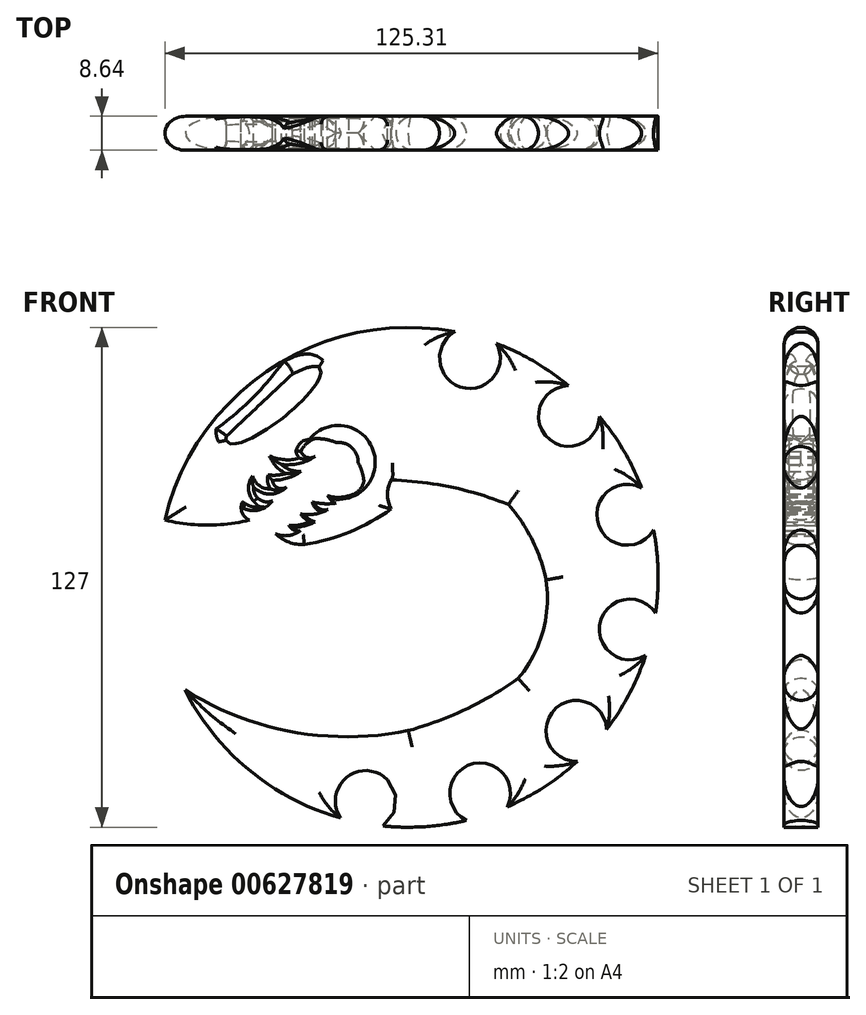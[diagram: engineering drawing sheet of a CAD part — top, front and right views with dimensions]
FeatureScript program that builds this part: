
annotation { "Feature Type Name" : "Feature", "Feature Type Description" : "" }
export const myFeature = defineFeature(function(context is Context, id is Id, definition is map)
    precondition{}
    {
        {
            var Q0;
            Q0=qCreatedBy(makeId("Front.planeOp"),FACE);
            var sketch = newSketch(context, id + "F0", { "sketchPlane" : qUnion([Q0])});
            skArc(sketch, "E0", {"start": v(11.85, 62.39) * mm, "mid": v(-34.6, 53.25) * mm, "end": v(-61.81, 14.54) * mm});
            skArc(sketch, "E1", {"start": v(11.85, 62.39) * mm, "mid": v(13.6, 48.25) * mm, "end": v(22.46, 59.4) * mm});
            skArc(sketch, "E2.1.0", {"start": v(40.75, 48.7) * mm, "mid": v(35.38, 35.5) * mm, "end": v(48.56, 40.92) * mm});
            skArc(sketch, "E2.2.0", {"start": v(59.32, 22.67) * mm, "mid": v(48.2, 13.76) * mm, "end": v(62.34, 12.07) * mm});
            skArc(sketch, "E2.3.0", {"start": v(62.84, -9.11) * mm, "mid": v(48.8, -11.47) * mm, "end": v(60.32, -19.85) * mm});
            skArc(sketch, "E2.4.0", {"start": v(50.43, -38.59) * mm, "mid": v(37.02, -33.8) * mm, "end": v(43, -46.73) * mm});
            skArc(sketch, "E2.5.0", {"start": v(25.23, -58.27) * mm, "mid": v(15.85, -47.55) * mm, "end": v(14.77, -61.76) * mm});
            skArc(sketch, "E2.6.0", {"start": v(-6.36, -63.18) * mm, "mid": v(-9.33, -49.25) * mm, "end": v(-17.2, -61.13) * mm});
            skLineSegment(sketch, "E2.anchor1", {"start": v(0, 0) * mm, "end": v(15.69, 55.68) * mm, "construction": true});
            skLineSegment(sketch, "E2.anchor2", {"start": v(0, 0) * mm, "end": v(-10.77, -56.84) * mm, "construction": true});
            skArc(sketch, "E3.trimOffspring", {"start": v(40.75, 48.7) * mm, "mid": v(32.05, 54.82) * mm, "end": v(22.46, 59.4) * mm});
            skArc(sketch, "E4.trimOffspring", {"start": v(59.32, 22.67) * mm, "mid": v(54.7, 32.25) * mm, "end": v(48.56, 40.92) * mm});
            skArc(sketch, "E5.trimOffspring", {"start": v(62.84, -9.11) * mm, "mid": v(63.48, 1.5) * mm, "end": v(62.34, 12.07) * mm});
            skArc(sketch, "E6.trimOffspring", {"start": v(50.43, -38.59) * mm, "mid": v(56.16, -29.63) * mm, "end": v(60.32, -19.85) * mm});
            skArc(sketch, "E7.trimOffspring", {"start": v(25.23, -58.27) * mm, "mid": v(34.6, -53.25) * mm, "end": v(43, -46.73) * mm});
            skArc(sketch, "E8.trimOffspring", {"start": v(-6.36, -63.18) * mm, "mid": v(4.26, -63.36) * mm, "end": v(14.77, -61.76) * mm});
            skPoint(sketch, "E9.endSnap0", {"position": v(-61.81, 14.54) * mm});
            skArc(sketch, "E10", {"start": v(-33.7, 11.06) * mm, "mid": v(-30.33, 8.93) * mm, "end": v(-26.4, 8.38) * mm});
            skArc(sketch, "E11", {"start": v(-11.26, 24.4) * mm, "mid": v(-15.29, 32.32) * mm, "end": v(-23.7, 35.21) * mm});
            skArc(sketch, "E12", {"start": v(-61.81, 14.54) * mm, "mid": v(-51.03, 13.27) * mm, "end": v(-40.25, 14.54) * mm});
            skPoint(sketch, "E12.endSnap0", {"position": v(-52.38, 14.54) * mm});
            skArc(sketch, "E13", {"start": v(-42.42, 17.84) * mm, "mid": v(-41.86, 15.84) * mm, "end": v(-40.25, 14.54) * mm});
            skArc(sketch, "E14", {"start": v(-42.42, 17.84) * mm, "mid": v(-38.16, 17.08) * mm, "end": v(-34.5, 19.4) * mm});
            skArc(sketch, "E15", {"start": v(-39.31, 22.94) * mm, "mid": v(-37.88, 19.85) * mm, "end": v(-34.5, 19.4) * mm});
            skArc(sketch, "E16", {"start": v(-39.31, 22.94) * mm, "mid": v(-35.13, 21.15) * mm, "end": v(-30.94, 22.94) * mm});
            skArc(sketch, "E17", {"start": v(-34.5, 24.67) * mm, "mid": v(-33.23, 22.76) * mm, "end": v(-30.94, 22.94) * mm});
            skArc(sketch, "E18", {"start": v(-34.5, 24.67) * mm, "mid": v(-30.67, 25.18) * mm, "end": v(-27.22, 26.94) * mm});
            skArc(sketch, "E19", {"start": v(-32.24, 28.7) * mm, "mid": v(-29.91, 27.3) * mm, "end": v(-27.22, 26.94) * mm});
            skArc(sketch, "E20", {"start": v(-32.24, 28.7) * mm, "mid": v(-27.78, 28.9) * mm, "end": v(-23.7, 30.7) * mm});
            skArc(sketch, "E21", {"start": v(-27.22, 32) * mm, "mid": v(-25.78, 30.5) * mm, "end": v(-23.7, 30.7) * mm});
            skPoint(sketch, "E9.end.orphan", {"position": v(-42.95, 14.54) * mm});
            skArc(sketch, "E22", {"start": v(-23.7, 35.21) * mm, "mid": v(-25.8, 33.98) * mm, "end": v(-27.22, 32) * mm});
            skEllipticalArc(sketch, "E23", {});
            skLineSegment(sketch, "E24", {"start": v(-46.15, 35.91) * mm, "end": v(-29.44, 51.63) * mm});
            skArc(sketch, "E25", {"start": v(-33.7, 11.06) * mm, "mid": v(-30.4, 10.62) * mm, "end": v(-27.33, 11.89) * mm});
            skArc(sketch, "E26", {"start": v(-30.22, 13.12) * mm, "mid": v(-29.01, 11.95) * mm, "end": v(-27.33, 11.89) * mm});
            skArc(sketch, "E27", {"start": v(-30.22, 13.12) * mm, "mid": v(-27.54, 13.33) * mm, "end": v(-24.95, 14.07) * mm});
            skArc(sketch, "E28", {"start": v(-27.33, 16.1) * mm, "mid": v(-26.24, 14.96) * mm, "end": v(-24.95, 14.07) * mm});
            skArc(sketch, "E29", {"start": v(-27.33, 16.1) * mm, "mid": v(-24.47, 15.96) * mm, "end": v(-21.68, 16.63) * mm});
            skArc(sketch, "E30", {"start": v(-24.36, 19.13) * mm, "mid": v(-23.42, 17.45) * mm, "end": v(-21.68, 16.63) * mm});
            skArc(sketch, "E31", {"start": v(-24.36, 19.13) * mm, "mid": v(-21.37, 18.7) * mm, "end": v(-18.35, 18.83) * mm});
            skPoint(sketch, "E32", {"position": v(-56.68, -28.62) * mm});
            skArc(sketch, "E33", {"start": v(-20.45, 20.72) * mm, "mid": v(-19.57, 19.59) * mm, "end": v(-18.35, 18.83) * mm});
            skArc(sketch, "E34", {"start": v(-20.45, 20.72) * mm, "mid": v(-17.77, 20.3) * mm, "end": v(-15.1, 20.72) * mm});
            skArc(sketch, "E35", {"start": v(-15.1, 20.72) * mm, "mid": v(-12.6, 21.96) * mm, "end": v(-11.26, 24.4) * mm});
            skArc(sketch, "E36", {"start": v(-56.68, -28.62) * mm, "mid": v(-29.34, -39.26) * mm, "end": v(0, -38.95) * mm});
            skArc(sketch, "E37", {"start": v(35.04, -0.67) * mm, "mid": v(31.48, 9.53) * mm, "end": v(25.45, 18.5) * mm});
            skArc(sketch, "E38", {"start": v(25.45, 18.5) * mm, "mid": v(10.84, 22.95) * mm, "end": v(-4.33, 24.71) * mm});
            skArc(sketch, "E39.trimOffspring", {"start": v(-56.68, -28.62) * mm, "mid": v(-40.36, -49.03) * mm, "end": v(-17.2, -61.13) * mm});
            skPoint(sketch, "E40.visualSharp", {"position": v(25.45, 18.5) * mm});
            skPoint(sketch, "E41.visualSharp", {"position": v(34.66, -19.7) * mm});
            skArc(sketch, "E42", {"start": v(27.93, -25.71) * mm, "mid": v(34.17, -13.96) * mm, "end": v(35.04, -0.67) * mm});
            skArc(sketch, "E43", {"start": v(0, -38.95) * mm, "mid": v(14.55, -33.56) * mm, "end": v(27.93, -25.71) * mm});
            skArc(sketch, "E44", {"start": v(-4.33, 24.71) * mm, "mid": v(-5.26, 21.05) * mm, "end": v(-4.33, 17.38) * mm});
            skArc(sketch, "E45", {"start": v(-26.4, 8.38) * mm, "mid": v(-14.81, 11.53) * mm, "end": v(-4.33, 17.38) * mm});
            const initialGuessF0  = {"E23": [-0.034181974582248115, 0.0437263421637328, -0.7832888515343989, -0.6216579244744834, 0.015090807915705154, 0.003951191540584326, 5.94360859800535, 4.104168110363256]};
            skSetInitialGuess(sketch, initialGuessF0);
            skSolve(sketch);
        }
        {
            var Q0;
            Q0 = qSketchRegion(id + "F0", true);
            extrude(context, id + "F1", {"entities" : qUnion([Q0]), "depth" : 25.4 * mm, "offsetDistance" : 25.4 * mm});
        }
        {
            var Q0;
            Q0=makeQuery(id+"F1.opExtrude","CAP_EDGE",EDGE,{"disambiguationData":[OSD([sQuery(id+"F0.wireOp",EDGE,"E0")])],"isStart":false});
            var Q1;
            Q1=makeQuery(id+"F1.opExtrude","CAP_EDGE",EDGE,{"disambiguationData":[OSD([sQuery(id+"F0.wireOp",EDGE,"E36")])],"isStart":false});
            var Q2;
            Q2=makeQuery(id+"F1.opExtrude","CAP_EDGE",EDGE,{"disambiguationData":[OSD([sQuery(id+"F0.wireOp",EDGE,"E37")])],"isStart":false});
            var Q3;
            Q3=makeQuery(id+"F1.opExtrude","CAP_EDGE",EDGE,{"disambiguationData":[OSD([sQuery(id+"F0.wireOp",EDGE,"E42")])],"isStart":false});
            var Q4;
            Q4=makeQuery(id+"F1.opExtrude","CAP_EDGE",EDGE,{"disambiguationData":[OSD([sQuery(id+"F0.wireOp",EDGE,"E43")])],"isStart":false});
            var Q5;
            Q5=makeQuery(id+"F1.opExtrude","CAP_EDGE",EDGE,{"disambiguationData":[OSD([sQuery(id+"F0.wireOp",EDGE,"E1")])],"isStart":false});
            var Q6;
            Q6=makeQuery(id+"F1.opExtrude","CAP_EDGE",EDGE,{"disambiguationData":[OSD([sQuery(id+"F0.wireOp",EDGE,"E3.trimOffspring")])],"isStart":false});
            var Q7;
            Q7=makeQuery(id+"F1.opExtrude","CAP_EDGE",EDGE,{"disambiguationData":[OSD([sQuery(id+"F0.wireOp",EDGE,"E2.1.0")])],"isStart":false});
            var Q8;
            Q8=makeQuery(id+"F1.opExtrude","CAP_EDGE",EDGE,{"disambiguationData":[OSD([sQuery(id+"F0.wireOp",EDGE,"E4.trimOffspring")])],"isStart":false});
            var Q9;
            Q9=makeQuery(id+"F1.opExtrude","CAP_EDGE",EDGE,{"disambiguationData":[OSD([sQuery(id+"F0.wireOp",EDGE,"E2.2.0")])],"isStart":false});
            var Q10;
            Q10=makeQuery(id+"F1.opExtrude","CAP_EDGE",EDGE,{"disambiguationData":[OSD([sQuery(id+"F0.wireOp",EDGE,"E2.3.0")])],"isStart":false});
            var Q11;
            Q11=makeQuery(id+"F1.opExtrude","CAP_EDGE",EDGE,{"disambiguationData":[OSD([sQuery(id+"F0.wireOp",EDGE,"E2.4.0")])],"isStart":false});
            var Q12;
            Q12=makeQuery(id+"F1.opExtrude","CAP_EDGE",EDGE,{"disambiguationData":[OSD([sQuery(id+"F0.wireOp",EDGE,"E6.trimOffspring")])],"isStart":false});
            var Q13;
            Q13=makeQuery(id+"F1.opExtrude","CAP_EDGE",EDGE,{"disambiguationData":[OSD([sQuery(id+"F0.wireOp",EDGE,"E7.trimOffspring")])],"isStart":false});
            var Q14;
            Q14=makeQuery(id+"F1.opExtrude","CAP_EDGE",EDGE,{"disambiguationData":[OSD([sQuery(id+"F0.wireOp",EDGE,"E2.6.0")])],"isStart":false});
            var Q15;
            Q15=makeQuery(id+"F1.opExtrude","CAP_EDGE",EDGE,{"disambiguationData":[OSD([sQuery(id+"F0.wireOp",EDGE,"E2.5.0")])],"isStart":false});
            var Q16;
            Q16=makeQuery(id+"F1.opExtrude","CAP_EDGE",EDGE,{"disambiguationData":[OSD([sQuery(id+"F0.wireOp",EDGE,"E12")])],"isStart":false});
            var Q17;
            Q17=makeQuery(id+"F1.opExtrude","CAP_EDGE",EDGE,{"disambiguationData":[OSD([sQuery(id+"F0.wireOp",EDGE,"E39.trimOffspring")])],"isStart":false});
            var Q18;
            Q18=makeQuery(id+"F1.opExtrude","CAP_EDGE",EDGE,{"disambiguationData":[OSD([sQuery(id+"F0.wireOp",EDGE,"E38")])],"isStart":false});
            fillet(context, id + "F2", {"entities" : qUnion([Q0, Q1, Q2, Q3, Q4, Q5, Q6, Q7, Q8, Q9, Q10, Q11, Q12, Q13, Q14, Q15, Q16, Q17, Q18]), "radius" : 4.32 * mm, "tangentPropagation" : true, "allowEdgeOverflow" : false});
        }
        {
            var Q0;
            Q0=makeQuery(id+"F1.opExtrude","CAP_EDGE",EDGE,{"disambiguationData":[OSD([sQuery(id+"F0.wireOp",EDGE,"E24")])],"isStart":false});
            var Q1;
            Q1=makeQuery(id+"F2.opFillet","BLEND_EDGE",EDGE,{"blendedFrom":[makeQuery(id+"F1.opExtrude","CAP_EDGE",EDGE,{"disambiguationData":[OSD([sQuery(id+"F0.wireOp",EDGE,"E0")])],"isStart":false}),makeQuery(id+"F1.opExtrude","SWEPT_FACE",FACE,{"disambiguationData":[OSD([sQuery(id+"F0.wireOp",EDGE,"E23")])]})],"blendedInto":[makeQuery(id+"F1.opExtrude","SWEPT_FACE",FACE,{"disambiguationData":[OSD([sQuery(id+"F0.wireOp",EDGE,"E23")])]})]});
            var Q2;
            Q2=makeQuery(id+"F1.opExtrude","CAP_EDGE",EDGE,{"disambiguationData":[OSD([sQuery(id+"F0.wireOp",EDGE,"E23")])],"isStart":false});
            var Q3;
            Q3=makeQuery(id+"F2.opFillet","BLEND_EDGE",EDGE,{"blendedFrom":[makeQuery(id+"F1.opExtrude","CAP_EDGE",EDGE,{"disambiguationData":[OSD([sQuery(id+"F0.wireOp",EDGE,"E0")])],"isStart":false}),makeQuery(id+"F1.opExtrude","SWEPT_FACE",FACE,{"disambiguationData":[OSD([sQuery(id+"F0.wireOp",EDGE,"E24")])]})],"blendedInto":[makeQuery(id+"F1.opExtrude","SWEPT_FACE",FACE,{"disambiguationData":[OSD([sQuery(id+"F0.wireOp",EDGE,"E24")])]})]});
            fillet(context, id + "F3", {"entities" : qUnion([Q0, Q1, Q2, Q3]), "radius" : 1.98 * mm, "tangentPropagation" : true, "allowEdgeOverflow" : false});
        }
        {
            var Q0;
            Q0=makeQuery(id+"F1.opExtrude","CAP_EDGE",EDGE,{"disambiguationData":[OSD([sQuery(id+"F0.wireOp",EDGE,"E16")])],"isStart":false});
            var Q1;
            Q1=makeQuery(id+"F1.opExtrude","CAP_EDGE",EDGE,{"disambiguationData":[OSD([sQuery(id+"F0.wireOp",EDGE,"E17")])],"isStart":false});
            var Q2;
            Q2=makeQuery(id+"F1.opExtrude","CAP_EDGE",EDGE,{"disambiguationData":[OSD([sQuery(id+"F0.wireOp",EDGE,"E18")])],"isStart":false});
            var Q3;
            Q3=makeQuery(id+"F1.opExtrude","CAP_EDGE",EDGE,{"disambiguationData":[OSD([sQuery(id+"F0.wireOp",EDGE,"E19")])],"isStart":false});
            var Q4;
            Q4=makeQuery(id+"F1.opExtrude","CAP_EDGE",EDGE,{"disambiguationData":[OSD([sQuery(id+"F0.wireOp",EDGE,"E20")])],"isStart":false});
            var Q5;
            Q5=makeQuery(id+"F1.opExtrude","CAP_EDGE",EDGE,{"disambiguationData":[OSD([sQuery(id+"F0.wireOp",EDGE,"E21")])],"isStart":false});
            var Q6;
            Q6=makeQuery(id+"F1.opExtrude","CAP_EDGE",EDGE,{"disambiguationData":[OSD([sQuery(id+"F0.wireOp",EDGE,"E15")])],"isStart":false});
            var Q7;
            Q7=makeQuery(id+"F2.opFillet","BLEND_EDGE",EDGE,{"blendedFrom":[makeQuery(id+"F1.opExtrude","CAP_EDGE",EDGE,{"disambiguationData":[OSD([sQuery(id+"F0.wireOp",EDGE,"E12")])],"isStart":false}),makeQuery(id+"F1.opExtrude","SWEPT_FACE",FACE,{"disambiguationData":[OSD([sQuery(id+"F0.wireOp",EDGE,"E14")])]})],"blendedInto":[makeQuery(id+"F1.opExtrude","SWEPT_FACE",FACE,{"disambiguationData":[OSD([sQuery(id+"F0.wireOp",EDGE,"E14")])]})]});
            var Q8;
            Q8=makeQuery(id+"F1.opExtrude","CAP_EDGE",EDGE,{"disambiguationData":[OSD([sQuery(id+"F0.wireOp",EDGE,"E22")])],"isStart":false});
            chamfer(context, id + "F4", {"entities" : qUnion([Q0, Q1, Q2, Q3, Q4, Q5, Q6, Q7, Q8]), "width" : 1.27 * mm, "tangentPropagation" : true});
        }
        {
            var Q0;
            Q0=makeQuery(id+"F1.opExtrude","CAP_EDGE",EDGE,{"disambiguationData":[OSD([sQuery(id+"F0.wireOp",EDGE,"E44")])],"isStart":false});
            var Q1;
            Q1=makeQuery(id+"F1.opExtrude","CAP_EDGE",EDGE,{"disambiguationData":[OSD([sQuery(id+"F0.wireOp",EDGE,"E45")])],"isStart":false});
            var Q2;
            Q2=makeQuery(id+"F1.opExtrude","CAP_EDGE",EDGE,{"disambiguationData":[OSD([sQuery(id+"F0.wireOp",EDGE,"E10")])],"isStart":false});
            fillet(context, id + "F5", {"entities" : qUnion([Q0, Q1, Q2]), "radius" : 2.54 * mm, "tangentPropagation" : true, "allowEdgeOverflow" : false});
        }
        {
            var Q0;
            Q0=makeQuery(id+"F1.opExtrude","CAP_EDGE",EDGE,{"disambiguationData":[OSD([sQuery(id+"F0.wireOp",EDGE,"E30")])],"isStart":false});
            var Q1;
            Q1=makeQuery(id+"F1.opExtrude","CAP_EDGE",EDGE,{"disambiguationData":[OSD([sQuery(id+"F0.wireOp",EDGE,"E28")])],"isStart":false});
            var Q2;
            Q2=makeQuery(id+"F1.opExtrude","CAP_EDGE",EDGE,{"disambiguationData":[OSD([sQuery(id+"F0.wireOp",EDGE,"E27")])],"isStart":false});
            var Q3;
            Q3=makeQuery(id+"F1.opExtrude","CAP_EDGE",EDGE,{"disambiguationData":[OSD([sQuery(id+"F0.wireOp",EDGE,"E34")])],"isStart":false});
            chamfer(context, id + "F6", {"entities" : qUnion([Q0, Q1, Q2, Q3]), "width" : 0.5 * mm, "tangentPropagation" : true});
        }
        {
            var Q0;
            Q0=qCreatedBy(makeId("Front.planeOp"),FACE);
            cPlane(context, id + "F7", {"entities" : qUnion([Q0]), "cplaneType" : CPlaneType.OFFSET, "offset" : 21.08 * mm, "width" : 152.4 * mm, "height" : 152.4 * mm});
        }
        {
            var Q0;
            Q0=qCreatedBy(id+"F7.planeOp",FACE);
            var sketch = newSketch(context, id + "F8", { "sketchPlane" : qUnion([Q0])});
            skCircle(sketch, "E46", {"center": v(2.29, 0) * mm, "radius": 121.2 * mm});
            skSolve(sketch);
        }
        {
            var Q0;
            Q0 = qSketchRegion(id + "F8", true);
            extrude(context, id + "F9", {"entities" : qUnion([Q0]), "operationType" : NewBodyOperationType.REMOVE, "oppositeDirection" : true, "depth" : 25.4 * mm, "offsetDistance" : 25.4 * mm});
        }
        {
            var Q0;
            Q0=makeQuery(id+"F1.opExtrude","SWEPT_BODY",BODY,{"disambiguationData":[OSD([sQuery(id+"F0.wireOp",EDGE,"E0"),sQuery(id+"F0.wireOp",EDGE,"E1"),sQuery(id+"F0.wireOp",EDGE,"E2.1.0"),sQuery(id+"F0.wireOp",EDGE,"E2.2.0"),sQuery(id+"F0.wireOp",EDGE,"E2.3.0"),sQuery(id+"F0.wireOp",EDGE,"E2.4.0"),sQuery(id+"F0.wireOp",EDGE,"E2.5.0"),sQuery(id+"F0.wireOp",EDGE,"E2.6.0"),sQuery(id+"F0.wireOp",EDGE,"E3.trimOffspring"),sQuery(id+"F0.wireOp",EDGE,"E4.trimOffspring"),sQuery(id+"F0.wireOp",EDGE,"E5.trimOffspring"),sQuery(id+"F0.wireOp",EDGE,"E6.trimOffspring"),sQuery(id+"F0.wireOp",EDGE,"E7.trimOffspring"),sQuery(id+"F0.wireOp",EDGE,"E8.trimOffspring"),sQuery(id+"F0.wireOp",EDGE,"E10"),sQuery(id+"F0.wireOp",EDGE,"E11"),sQuery(id+"F0.wireOp",EDGE,"E12"),sQuery(id+"F0.wireOp",EDGE,"E13"),sQuery(id+"F0.wireOp",EDGE,"E14"),sQuery(id+"F0.wireOp",EDGE,"E15"),sQuery(id+"F0.wireOp",EDGE,"E16"),sQuery(id+"F0.wireOp",EDGE,"E17"),sQuery(id+"F0.wireOp",EDGE,"E18"),sQuery(id+"F0.wireOp",EDGE,"E19"),sQuery(id+"F0.wireOp",EDGE,"E20"),sQuery(id+"F0.wireOp",EDGE,"E21"),sQuery(id+"F0.wireOp",EDGE,"E22"),sQuery(id+"F0.wireOp",EDGE,"E23"),sQuery(id+"F0.wireOp",EDGE,"E24"),sQuery(id+"F0.wireOp",EDGE,"E25"),sQuery(id+"F0.wireOp",EDGE,"E26"),sQuery(id+"F0.wireOp",EDGE,"E27"),sQuery(id+"F0.wireOp",EDGE,"E28"),sQuery(id+"F0.wireOp",EDGE,"E29"),sQuery(id+"F0.wireOp",EDGE,"E30"),sQuery(id+"F0.wireOp",EDGE,"E31"),sQuery(id+"F0.wireOp",EDGE,"E33"),sQuery(id+"F0.wireOp",EDGE,"E34"),sQuery(id+"F0.wireOp",EDGE,"E35"),sQuery(id+"F0.wireOp",EDGE,"E36"),sQuery(id+"F0.wireOp",EDGE,"E37"),sQuery(id+"F0.wireOp",EDGE,"E38"),sQuery(id+"F0.wireOp",EDGE,"E39.trimOffspring"),sQuery(id+"F0.wireOp",EDGE,"E42"),sQuery(id+"F0.wireOp",EDGE,"E43"),sQuery(id+"F0.wireOp",EDGE,"E44"),sQuery(id+"F0.wireOp",EDGE,"E45")])]});
            var Q1;
            Q1=makeQuery(id+"F9.boolean.opBoolean","COPY",FACE,{"derivedFrom":makeQuery(id+"F9.opExtrude","CAP_FACE",FACE,{"disambiguationData":[OSD([sQuery(id+"F8.wireOp",EDGE,"E46")])],"isStart":true})});
            mirror(context, id + "F10", {"operationType" : NewBodyOperationType.ADD, "entities" : qUnion([Q0]), "mirrorPlane" : qUnion([Q1])});
        }
    });
